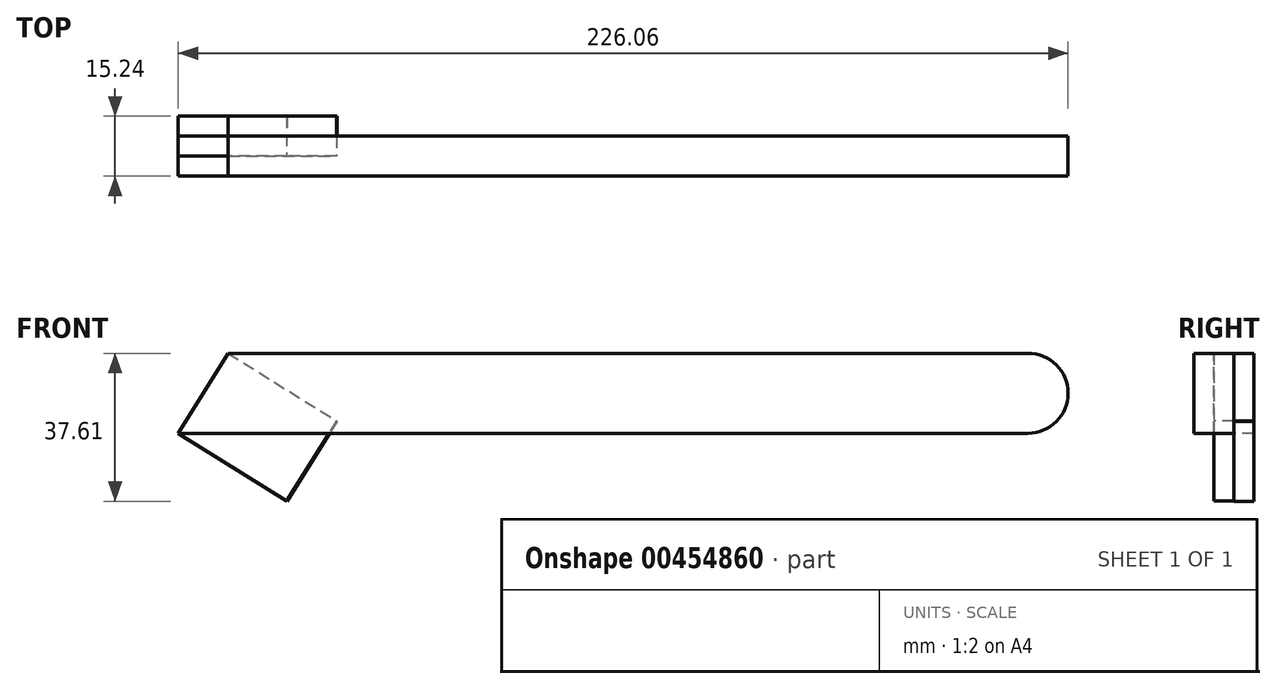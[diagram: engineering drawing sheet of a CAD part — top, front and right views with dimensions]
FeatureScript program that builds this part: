
annotation { "Feature Type Name" : "Feature", "Feature Type Description" : "" }
export const myFeature = defineFeature(function(context is Context, id is Id, definition is map)
    precondition{}
    {
        {
            var Q0;
            Q0=qCreatedBy(makeId("Front.planeOp"),FACE);
            var sketch = newSketch(context, id + "F0", { "sketchPlane" : qUnion([Q0])});
            skCircle(sketch, "E0", {"center": v(0, 0) * mm, "radius": 10.16 * mm});
            skLineSegment(sketch, "E1.bottom", {"start": v(0, 10.16) * mm, "end": v(-203.2, 10.16) * mm});
            skLineSegment(sketch, "E1.top", {"start": v(0, -10.16) * mm, "end": v(-203.2, -10.16) * mm});
            skLineSegment(sketch, "E1.left", {"start": v(0, 10.16) * mm, "end": v(0, -10.16) * mm});
            skLineSegment(sketch, "E1.right", {"start": v(-203.2, 10.16) * mm, "end": v(-203.2, -10.16) * mm});
            skLineSegment(sketch, "E2", {"start": v(-215.9, -10.16) * mm, "end": v(-203.2, -10.16) * mm});
            skLineSegment(sketch, "E3", {"start": v(-215.9, -10.16) * mm, "end": v(-203.2, 10.16) * mm});
            skLineSegment(sketch, "E4", {"start": v(-203.2, 10.16) * mm, "end": v(-175.68, -7.05) * mm});
            skLineSegment(sketch, "E5", {"start": v(-175.68, -7.05) * mm, "end": v(-188.38, -27.37) * mm});
            skLineSegment(sketch, "E6", {"start": v(-188.38, -27.37) * mm, "end": v(-215.9, -10.16) * mm});
            skLineSegment(sketch, "E7", {"start": v(-188.38, -27.37) * mm, "end": v(-140.59, -10.16) * mm});
            skSolve(sketch);
        }
        {
            var Q0;
            Q0=makeQuery(id+"F0.imprint","IMPRINT",FACE,{"disambiguationData":[TD([[makeQuery(id+"F0.imprint","IMPRINT",EDGE,{"derivedFrom":sQuery(id+"F0.wireOp",EDGE,"E0")}),1.0]])]});
            extrude(context, id + "F1", {"entities" : qUnion([Q0]), "endBound" : BoundingType.SYMMETRIC, "depth" : 10.16 * mm, "offsetDistance" : 25.4 * mm});
        }
        {
            var Q0;
            {var subQ1=sQuery(id+"F0.wireOp",EDGE,"E1.bottom");Q0=makeQuery(id+"F0.imprint","IMPRINT",FACE,{"disambiguationData":[TD([[makeQuery(id+"F0.imprint","IMPRINT",EDGE,{"derivedFrom":subQ1}),1.0]])]});}
            var Q1;
            Q1=makeQuery(id+"F0.imprint","IMPRINT",FACE,{"disambiguationData":[TD([[makeQuery(id+"F0.imprint","IMPRINT",EDGE,{"derivedFrom":sQuery(id+"F0.wireOp",EDGE,"E1.right")}),-1.0]])]});
            var Q2;
            {var subQ0=sQuery(id+"F0.wireOp",EDGE,"E1.right");Q2=makeQuery(id+"F0.imprint","IMPRINT",FACE,{"disambiguationData":[TD([[makeQuery(id+"F0.imprint","IMPRINT",EDGE,{"derivedFrom":subQ0}),1.0]])]});}
            extrude(context, id + "F2", {"entities" : qUnion([Q0, Q1, Q2]), "operationType" : NewBodyOperationType.ADD, "endBound" : BoundingType.SYMMETRIC, "depth" : 10.16 * mm, "offsetDistance" : 25.4 * mm});
        }
        {
            var Q0;
            {var subQ0=sQuery(id+"F0.wireOp",EDGE,"E0");Q0=makeQuery(id+"F2.boolean.opBoolean","MERGE",FACE,{"derivedFrom":[makeQuery(id+"F1.opExtrude","CAP_FACE",FACE,{"disambiguationData":[OSD([subQ0])],"isStart":true}),makeQuery(id+"F2.opExtrude","CAP_FACE",FACE,{"disambiguationData":[OSD([subQ0,sQuery(id+"F0.wireOp",EDGE,"E1.bottom"),sQuery(id+"F0.wireOp",EDGE,"E1.top"),sQuery(id+"F0.wireOp",EDGE,"E2"),sQuery(id+"F0.wireOp",EDGE,"E3")])],"isStart":true})]});}
            var sketch = newSketch(context, id + "F3", { "sketchPlane" : qUnion([Q0])});
            skLineSegment(sketch, "E8", {"start": v(215.9, -10.16) * mm, "end": v(203.2, 10.16) * mm});
            skLineSegment(sketch, "E9", {"start": v(203.2, 10.16) * mm, "end": v(175.54, -7.13) * mm});
            skLineSegment(sketch, "E10", {"start": v(175.54, -7.13) * mm, "end": v(188.25, -27.45) * mm});
            skLineSegment(sketch, "E11", {"start": v(188.25, -27.45) * mm, "end": v(215.9, -10.16) * mm});
            skSolve(sketch);
        }
        {
            var Q0;
            Q0 = qSketchRegion(id + "F3", true);
            extrude(context, id + "F4", {"entities" : qUnion([Q0]), "depth" : 5.08 * mm, "offsetDistance" : 25.4 * mm});
        }
        {
            var Q0;
            Q0=makeQuery(id+"F0.imprint","IMPRINT",FACE,{"disambiguationData":[TD([[makeQuery(id+"F0.imprint","IMPRINT",EDGE,{"derivedFrom":sQuery(id+"F0.wireOp",EDGE,"E1.right")}),-1.0]])]});
            var Q1;
            {var subQ0=sQuery(id+"F0.wireOp",EDGE,"E2");Q1=makeQuery(id+"F0.imprint","IMPRINT",FACE,{"disambiguationData":[TD([[makeQuery(id+"F0.imprint","IMPRINT",EDGE,{"derivedFrom":subQ0}),-1.0]])]});}
            var Q2;
            {var subQ0=sQuery(id+"F0.wireOp",EDGE,"E1.right");Q2=makeQuery(id+"F0.imprint","IMPRINT",FACE,{"disambiguationData":[TD([[makeQuery(id+"F0.imprint","IMPRINT",EDGE,{"derivedFrom":subQ0}),1.0]])]});}
            extrude(context, id + "F5", {"entities" : qUnion([Q0, Q1, Q2]), "oppositeDirection" : true, "depth" : 10.16 * mm, "offsetDistance" : 25.4 * mm});
        }
    });
